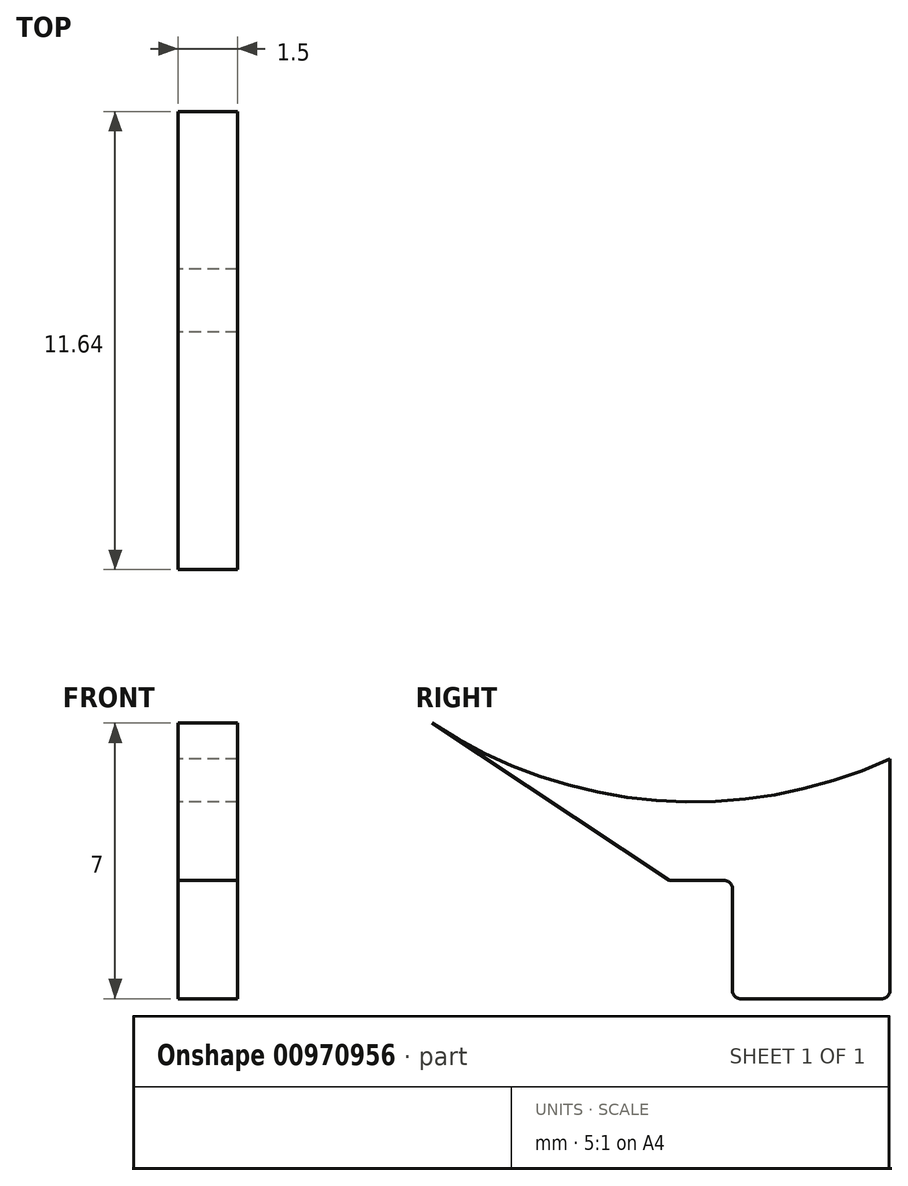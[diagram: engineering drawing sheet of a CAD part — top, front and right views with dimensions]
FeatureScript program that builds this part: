
annotation { "Feature Type Name" : "Feature", "Feature Type Description" : "" }
export const myFeature = defineFeature(function(context is Context, id is Id, definition is map)
    precondition{}
    {
        {
            var Q0;
            Q0=qCreatedBy(makeId("Right.planeOp"),FACE);
            var sketch = newSketch(context, id + "F0", { "sketchPlane" : qUnion([Q0])});
            skPoint(sketch, "E0.middle", {"position": v(0, 0) * mm});
            skLineSegment(sketch, "E1.0", {"start": v(-22.3, 5.1) * mm, "end": v(-22.3, -0.8) * mm});
            skCircle(sketch, "E2", {"center": v(-27.3, 16) * mm, "radius": 1 * mm});
            skLineSegment(sketch, "E3", {"start": v(-26.3, -0.8) * mm, "end": v(-26.3, 1.8) * mm});
            skLineSegment(sketch, "E4", {"start": v(-26.5, 2) * mm, "end": v(-27.9, 2) * mm});
            skLineSegment(sketch, "E5.0", {"start": v(20.24, 30) * mm, "end": v(-30.7, 30) * mm});
            skLineSegment(sketch, "E6.0", {"start": v(22.5, 0.2) * mm, "end": v(22.5, 1.8) * mm});
            skLineSegment(sketch, "E7.0", {"start": v(22.3, 2) * mm, "end": v(21, 2) * mm});
            skPoint(sketch, "E8.visualSharp", {"position": v(-19.5, 25.2) * mm});
            skPoint(sketch, "E9.visualSharp", {"position": v(25.81, 0.04) * mm});
            skPoint(sketch, "E10.visualSharp", {"position": v(-24.15, 33.62) * mm});
            skLineSegment(sketch, "E11", {"start": v(0, 0.86) * mm, "end": v(0, 30) * mm, "construction": true});
            skLineSegment(sketch, "E12.top", {"start": v(23.81, -2) * mm, "end": v(20.2, -2) * mm});
            skLineSegment(sketch, "E12.left", {"start": v(25.81, 0) * mm, "end": v(25.81, 0) * mm});
            skPoint(sketch, "E13.visualSharp", {"position": v(22.5, 2) * mm});
            skArc(sketch, "E13.filletArc", {"start": v(22.5, 1.8) * mm, "mid": v(22.44, 1.94) * mm, "end": v(22.3, 2) * mm});
            skPoint(sketch, "E14.visualSharp", {"position": v(25.81, -2) * mm});
            skArc(sketch, "E14.filletArc", {"start": v(23.81, -2) * mm, "mid": v(25.22, -1.41) * mm, "end": v(25.81, 0) * mm});
            skLineSegment(sketch, "E15", {"start": v(20, -1.8) * mm, "end": v(20, -0.2) * mm});
            skLineSegment(sketch, "E16", {"start": v(22.3, 0) * mm, "end": v(20.2, 0) * mm});
            skPoint(sketch, "E17.visualSharp", {"position": v(22.5, 0) * mm});
            skArc(sketch, "E17.filletArc", {"start": v(22.3, 0) * mm, "mid": v(22.44, 0.06) * mm, "end": v(22.5, 0.2) * mm});
            skPoint(sketch, "E18.visualSharp", {"position": v(20, 0) * mm});
            skArc(sketch, "E18.filletArc", {"start": v(20.2, 0) * mm, "mid": v(20.06, -0.06) * mm, "end": v(20, -0.2) * mm});
            skPoint(sketch, "E19.visualSharp", {"position": v(20, -2) * mm});
            skArc(sketch, "E19.filletArc", {"start": v(20, -1.8) * mm, "mid": v(20.06, -1.94) * mm, "end": v(20.2, -2) * mm});
            skArc(sketch, "E20.filletArc", {"start": v(25.81, 0) * mm, "mid": v(25.8, 0.04) * mm, "end": v(25.8, 0.07) * mm});
            skLineSegment(sketch, "E21", {"start": v(-26.1, -1) * mm, "end": v(-22.5, -1) * mm});
            skPoint(sketch, "E22.visualSharp", {"position": v(-26.3, 2) * mm});
            skArc(sketch, "E22.filletArc", {"start": v(-26.3, 1.8) * mm, "mid": v(-26.36, 1.94) * mm, "end": v(-26.5, 2) * mm});
            skPoint(sketch, "E23.visualSharp", {"position": v(-26.3, -1) * mm});
            skArc(sketch, "E23.filletArc", {"start": v(-26.3, -0.8) * mm, "mid": v(-26.24, -0.94) * mm, "end": v(-26.1, -1) * mm});
            skPoint(sketch, "E24.visualSharp", {"position": v(-22.3, -1) * mm});
            skArc(sketch, "E24.filletArc", {"start": v(-22.5, -1) * mm, "mid": v(-22.36, -0.94) * mm, "end": v(-22.3, -0.8) * mm});
            skLineSegment(sketch, "E25.0", {"start": v(-27.3, 29.69) * mm, "end": v(-27.3, -0.8) * mm, "construction": true});
            skCircle(sketch, "E26", {"center": v(-27.3, 16) * mm, "radius": 12 * mm});
            skLineSegment(sketch, "E27", {"start": v(-27.9, 2) * mm, "end": v(-33.94, 6) * mm});
            skLineSegment(sketch, "E28", {"start": v(-36.12, 24.14) * mm, "end": v(-30.7, 30) * mm});
            skLineSegment(sketch, "E29", {"start": v(21, 2) * mm, "end": v(21, 2.82) * mm});
            skLineSegment(sketch, "E30", {"start": v(21, 2.82) * mm, "end": v(16.7, 26) * mm});
            skLineSegment(sketch, "E31", {"start": v(25.81, 0.04) * mm, "end": v(20.24, 30) * mm});
            skLineSegment(sketch, "E32.0", {"start": v(16.7, 26) * mm, "end": v(-20.67, 26) * mm});
            skSolve(sketch);
        }
        {
            var Q0;
            Q0=makeQuery(id+"F0.imprint","IMPRINT",FACE,{"disambiguationData":[TD([[makeQuery(id+"F0.imprint","IMPRINT",EDGE,{"derivedFrom":sQuery(id+"F0.wireOp",EDGE,"E0.bottom")}),1.0]])]});
            var Q1;
            Q1=makeQuery(id+"F0.imprint","IMPRINT",FACE,{"disambiguationData":[TD([[makeQuery(id+"F0.imprint","IMPRINT",EDGE,{"derivedFrom":sQuery(id+"F0.wireOp",EDGE,"E1.0")}),-1.0]])]});
            extrude(context, id + "F1", {"entities" : qUnion([Q0, Q1]), "depth" : 1.5 * mm, "offsetDistance" : 25 * mm, "symmetric" : true});
        }
    });
